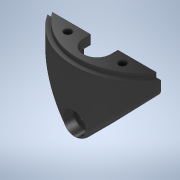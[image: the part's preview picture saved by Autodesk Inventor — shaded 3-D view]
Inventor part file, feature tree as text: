
AUTODESK INVENTOR PART (.ipt)
format: ipt  version: 2020 (Build 240168000, 168)  size: 342,528 bytes
history: native  units: in
note: dims shown in document units (in); Inventor stores cm internally (conversion verified against a paired STEP export)
features: sketch x7, extrude x3, hole x3, revolve x2, plane x2, fillet x2
ambient origin geometry x8: Origin, YZ Plane, XZ Plane, XY Plane, X Axis, Y Axis, Z Axis, Center Point
bodies: Solid1 (feature_tree)
feature tree (19):
  sketch  "Sketch1"  dims[d2=1.74in d3=0.126in]
  revolve  "Revolution1"  [1 undecoded]
  extrude  "Extrusion1"  Depth=0.25in
  extrude  "Extrusion3"  Depth=1.0in
  plane  "Work Plane3"
  hole  "Hole3"  [1 undecoded]
  plane  "Work Plane6"
  hole  "Hole5"  [1 undecoded]
  revolve  "Revolution2"  [1 undecoded]
  extrude  "Extrusion13"  Depth=0.375in
  fillet  "Fillet3"  Radius=0.375in
  fillet  "Fillet1"  Radius=1.2in
  hole  "Hole6"  [1 undecoded]
  sketch  "Sketch2"  dims[d5=0.25in d7=0.25in]
  sketch  "Sketch9"  dims[d9=180.0deg d10=1.0in]
  sketch  "Sketch19"  dims[d11=1.85in d12=0.0in d16=1.382in d17=0.0in]
  sketch  "Sketch20"  dims[d46=1.25in d47=1.5in]
  sketch  "Sketch21"  dims[d48=0.205in d49=0.75in d50=0.3438in d51=1.0in d52=0.5635in d53=1.0in d54=0.8108in d76=0.0312in]
  sketch  "Sketch23"  dims[d85=1.375in d86=0.266in d87=0.75in d88=0.625in d89=0.313in d90=0.5635in d91=1.0in d92=0.8108in d93=0.375in d95=0.375in d99=1.2in d102=90.0deg d103=0.2in d104=0.0in d110=0.125in d111=0.5in d112=0.2184in d113=0.4359in d114=0.5625in d115=0.25in d116=0.51in d119=0.35in d120=0.75in d121=0.51in d122=0.188in d123=0.5635in d124=0.25in d125=0.0in d126=1.85in d117=0.5635in d118=0.75in]
note: 5 required parameter values undecoded (feature->parameter linkage not recoverable at this tier; creation-order binding heuristic only, values carry confidence <= 0.55)